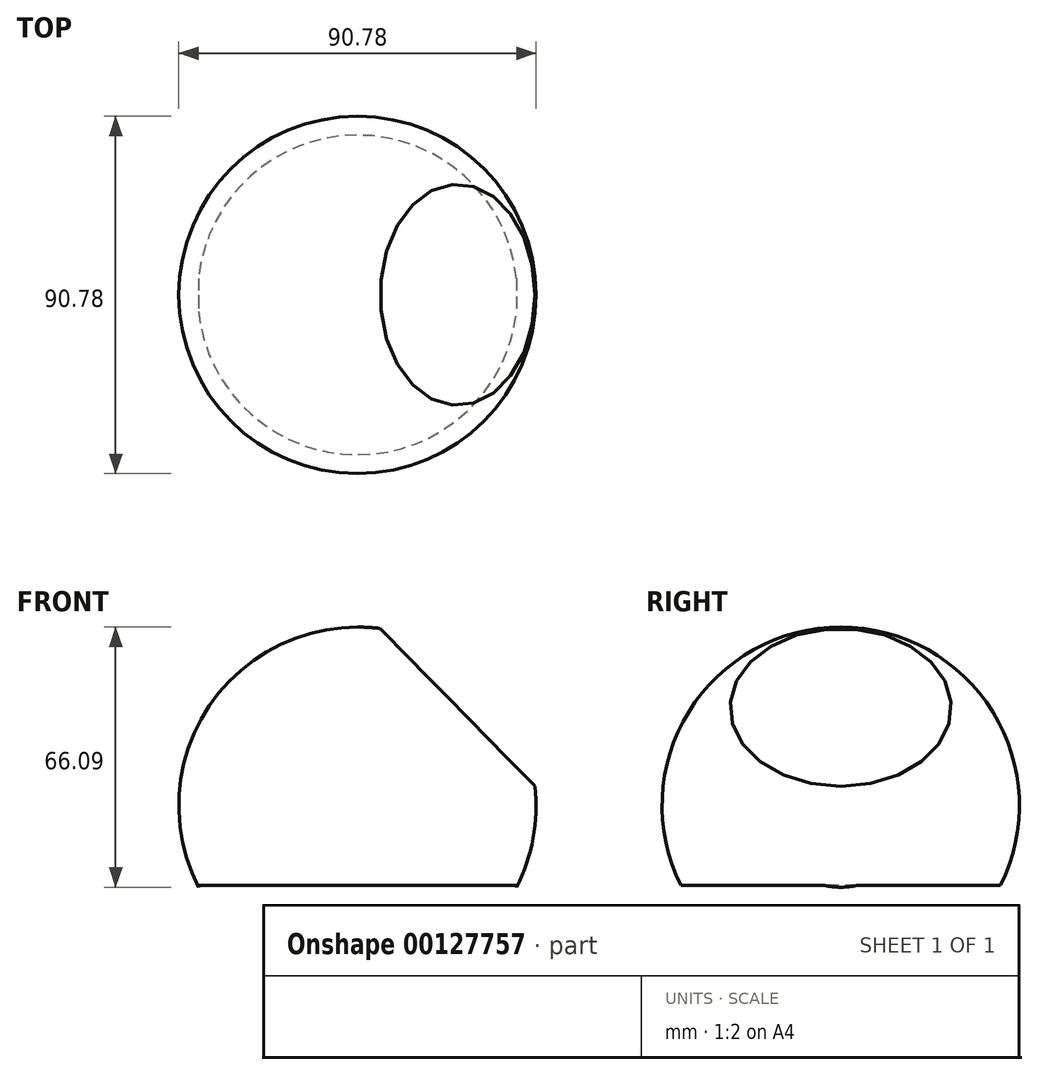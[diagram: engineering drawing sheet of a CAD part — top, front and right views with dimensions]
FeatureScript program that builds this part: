
annotation { "Feature Type Name" : "Feature", "Feature Type Description" : "" }
export const myFeature = defineFeature(function(context is Context, id is Id, definition is map)
    precondition{}
    {
        {
            var Q0;
            Q0=qCreatedBy(makeId("Front.planeOp"),FACE);
            var sketch = newSketch(context, id + "F0", { "sketchPlane" : qUnion([Q0])});
            skArc(sketch, "E0", {"start": v(0, -45.4) * mm, "mid": v(45.4, 0) * mm, "end": v(0, 45.4) * mm});
            skLineSegment(sketch, "E1", {"start": v(0, 45.4) * mm, "end": v(0, -45.4) * mm});
            skSolve(sketch);
        }
        {
            var Q0;
            Q0=qCreatedBy(makeId("Front.planeOp"),FACE);
            var sketch = newSketch(context, id + "F1", { "sketchPlane" : qUnion([Q0])});
            skLineSegment(sketch, "E2", {"start": v(0, 74.85) * mm, "end": v(0, -75.2) * mm, "construction": true});
            skSolve(sketch);
        }
        {
            var Q0;
            Q0=makeQuery(id+"F0.imprint","IMPRINT",FACE,{"disambiguationData":[TD([[makeQuery(id+"F0.imprint","IMPRINT",EDGE,{"derivedFrom":sQuery(id+"F0.wireOp",EDGE,"E0")}),1.0]])]});
            var Q1;
            Q1=sQuery(id+"F1.wireOp",EDGE,"E2");
            revolve(context, id + "F2", {"entities" : qUnion([Q0]), "axis" : qUnion([Q1]), "revolveType" : RevolveType.FULL});
        }
        {
            var Q0;
            Q0=qCreatedBy(makeId("Front.planeOp"),FACE);
            var sketch = newSketch(context, id + "F3", { "sketchPlane" : qUnion([Q0])});
            skLineSegment(sketch, "E3", {"start": v(0, 53.42) * mm, "end": v(0, -69.36) * mm, "construction": true});
            skLineSegment(sketch, "E4.bottom", {"start": v(-40.4, -20.28) * mm, "end": v(0, -20.28) * mm});
            skLineSegment(sketch, "E4.top", {"start": v(-40.4, -45.97) * mm, "end": v(0, -45.97) * mm});
            skLineSegment(sketch, "E4.left", {"start": v(-40.4, -20.28) * mm, "end": v(-40.4, -45.97) * mm});
            skLineSegment(sketch, "E5.MirrorCS", {"start": v(40.4, -20.28) * mm, "end": v(0, -20.28) * mm});
            skLineSegment(sketch, "E6.MirrorCS", {"start": v(40.4, -45.97) * mm, "end": v(0, -45.97) * mm});
            skLineSegment(sketch, "E7.MirrorCS", {"start": v(40.4, -20.28) * mm, "end": v(40.4, -45.97) * mm});
            skSolve(sketch);
        }
        {
            var Q0;
            Q0 = qSketchRegion(id + "F3", true);
            extrude(context, id + "F4", {"entities" : qUnion([Q0]), "operationType" : NewBodyOperationType.REMOVE, "endBound" : BoundingType.THROUGH_ALL, "oppositeDirection" : true, "depth" : 25 * mm, "hasSecondDirection" : true, "secondDirectionBound" : SecondDirectionBoundingType.THROUGH_ALL, "secondDirectionOppositeDirection" : false, "secondDirectionDepth" : 25 * mm});
        }
        {
            var Q0;
            Q0=qCreatedBy(makeId("Front.planeOp"),FACE);
            var sketch = newSketch(context, id + "F5", { "sketchPlane" : qUnion([Q0])});
            skLineSegment(sketch, "E8", {"start": v(4.3, 46.53) * mm, "end": v(47.91, 2.08) * mm});
            skLineSegment(sketch, "E9", {"start": v(4.3, 46.53) * mm, "end": v(9.36, 46.53) * mm});
            skLineSegment(sketch, "E10", {"start": v(9.36, 46.53) * mm, "end": v(50.44, 46.53) * mm});
            skLineSegment(sketch, "E11", {"start": v(47.91, 2.08) * mm, "end": v(50.44, 46.53) * mm});
            skSolve(sketch);
        }
        {
            var Q0;
            Q0=makeQuery(id+"F5.imprint","IMPRINT",FACE,{"disambiguationData":[TD([[makeQuery(id+"F5.imprint","IMPRINT",EDGE,{"derivedFrom":sQuery(id+"F5.wireOp",EDGE,"E8")}),1.0]])]});
            extrude(context, id + "F6", {"entities" : qUnion([Q0]), "operationType" : NewBodyOperationType.REMOVE, "endBound" : BoundingType.THROUGH_ALL, "depth" : 25 * mm});
        }
        {
            var Q0;
            Q0=makeQuery(id+"F5.imprint","IMPRINT",FACE,{"disambiguationData":[TD([[makeQuery(id+"F5.imprint","IMPRINT",EDGE,{"derivedFrom":sQuery(id+"F5.wireOp",EDGE,"E8")}),1.0]])]});
            extrude(context, id + "F7", {"entities" : qUnion([Q0]), "operationType" : NewBodyOperationType.REMOVE, "endBound" : BoundingType.THROUGH_ALL, "oppositeDirection" : true, "depth" : 25 * mm});
        }
    });
